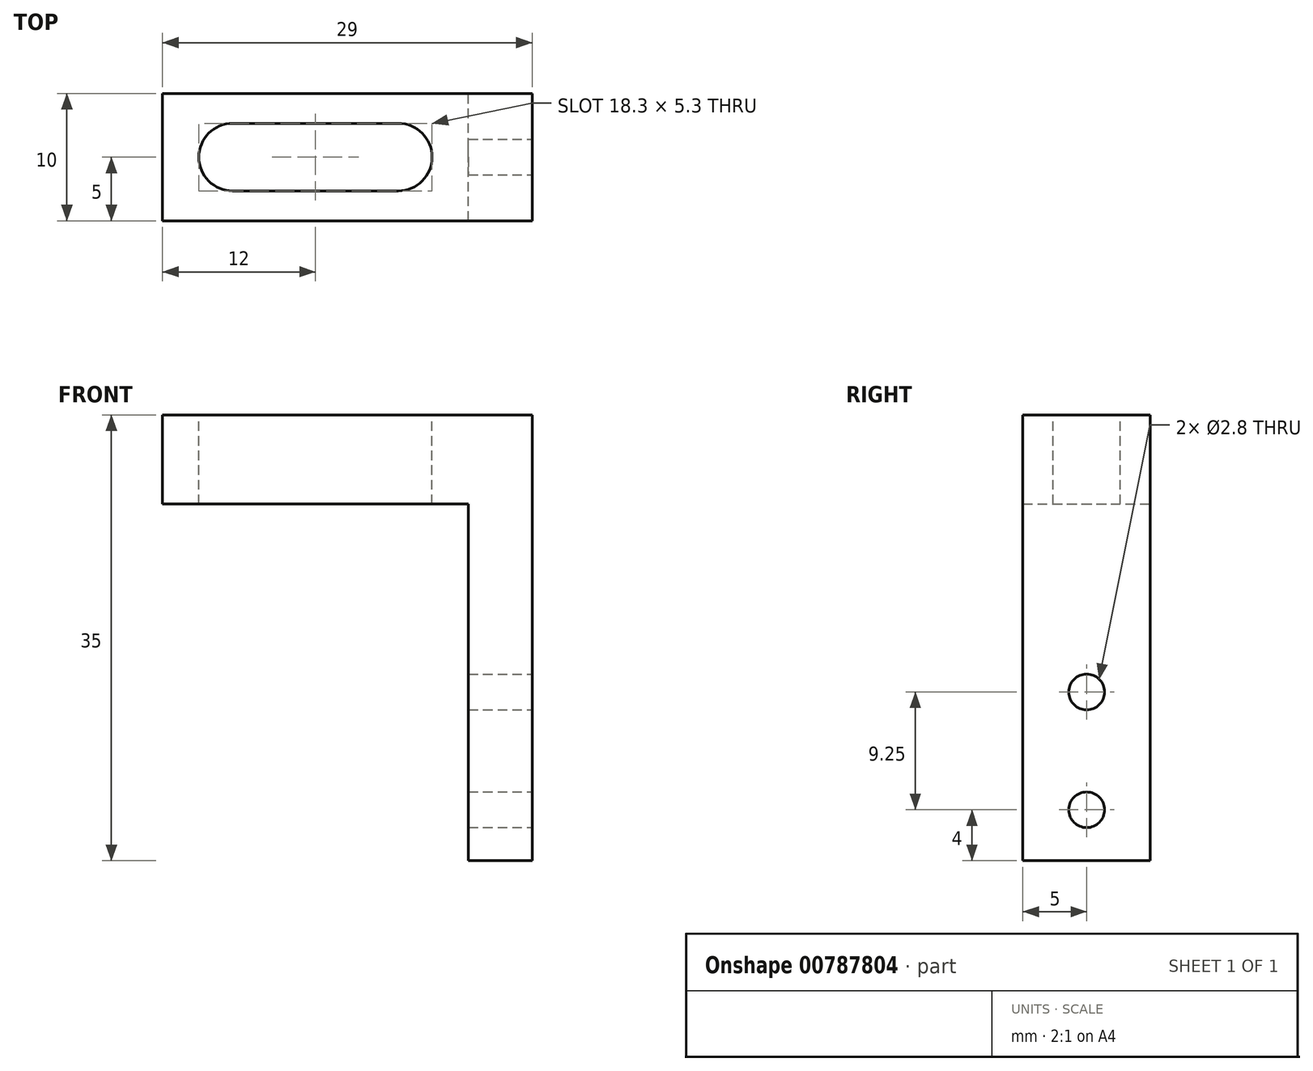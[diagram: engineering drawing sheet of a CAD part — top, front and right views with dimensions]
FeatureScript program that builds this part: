
annotation { "Feature Type Name" : "Feature", "Feature Type Description" : "" }
export const myFeature = defineFeature(function(context is Context, id is Id, definition is map)
    precondition{}
    {
        {
            var Q0;
            Q0=qCreatedBy(makeId("Front.planeOp"),FACE);
            var sketch = newSketch(context, id + "F0", { "sketchPlane" : qUnion([Q0])});
            skLineSegment(sketch, "E0", {"start": v(0, 0) * mm, "end": v(29, 0) * mm});
            skLineSegment(sketch, "E1", {"start": v(29, 0) * mm, "end": v(29, -35) * mm});
            skLineSegment(sketch, "E2", {"start": v(29, -35) * mm, "end": v(24, -35) * mm});
            skLineSegment(sketch, "E3", {"start": v(24, -35) * mm, "end": v(24, -7) * mm});
            skLineSegment(sketch, "E4", {"start": v(24, -7) * mm, "end": v(0, -7) * mm});
            skLineSegment(sketch, "E5", {"start": v(0, -7) * mm, "end": v(0, 0) * mm});
            skSolve(sketch);
        }
        {
            var Q0;
            Q0=makeQuery(id+"F0.imprint","IMPRINT",FACE,{"disambiguationData":[TD([[makeQuery(id+"F0.imprint","IMPRINT",EDGE,{"derivedFrom":sQuery(id+"F0.wireOp",EDGE,"E0")}),-1.0]])]});
            extrude(context, id + "F1", {"entities" : qUnion([Q0]), "depth" : 10 * mm, "offsetDistance" : 25 * mm});
        }
        {
            var Q0;
            Q0=makeQuery(id+"F1.opExtrude","SWEPT_FACE",FACE,{"disambiguationData":[OSD([sQuery(id+"F0.wireOp",EDGE,"E0")])]});
            var sketch = newSketch(context, id + "F2", { "sketchPlane" : qUnion([Q0])});
            skLineSegment(sketch, "E6.bottom", {"start": v(5.5, -7.65) * mm, "end": v(18.5, -7.65) * mm});
            skLineSegment(sketch, "E6.top", {"start": v(5.5, -2.35) * mm, "end": v(18.5, -2.35) * mm});
            skLineSegment(sketch, "E6.left", {"start": v(5.5, -7.65) * mm, "end": v(5.5, -2.35) * mm});
            skLineSegment(sketch, "E6.right", {"start": v(18.5, -7.65) * mm, "end": v(18.5, -2.35) * mm});
            skArc(sketch, "E7", {"start": v(5.5, -2.35) * mm, "mid": v(2.85, -5) * mm, "end": v(5.5, -7.65) * mm});
            skArc(sketch, "E8", {"start": v(18.5, -7.65) * mm, "mid": v(21.15, -5) * mm, "end": v(18.5, -2.35) * mm});
            skSolve(sketch);
        }
        {
            var Q0;
            Q0=makeQuery(id+"F2.imprint","IMPRINT",FACE,{"disambiguationData":[TD([[makeQuery(id+"F2.imprint","IMPRINT",EDGE,{"derivedFrom":sQuery(id+"F2.wireOp",EDGE,"E6.bottom")}),1.0]])]});
            var Q1;
            Q1=makeQuery(id+"F2.imprint","IMPRINT",FACE,{"disambiguationData":[TD([[makeQuery(id+"F2.imprint","IMPRINT",EDGE,{"derivedFrom":sQuery(id+"F2.wireOp",EDGE,"E6.left")}),1.0]])]});
            var Q2;
            Q2=makeQuery(id+"F2.imprint","IMPRINT",FACE,{"disambiguationData":[TD([[makeQuery(id+"F2.imprint","IMPRINT",EDGE,{"derivedFrom":sQuery(id+"F2.wireOp",EDGE,"E6.right")}),-1.0]])]});
            extrude(context, id + "F3", {"entities" : qUnion([Q0, Q1, Q2]), "operationType" : NewBodyOperationType.REMOVE, "endBound" : BoundingType.UP_TO_NEXT, "oppositeDirection" : true, "depth" : 25 * mm, "offsetDistance" : 25 * mm});
        }
        {
            var Q0;
            Q0=makeQuery(id+"F1.opExtrude","SWEPT_FACE",FACE,{"disambiguationData":[OSD([sQuery(id+"F0.wireOp",EDGE,"E1")])]});
            var sketch = newSketch(context, id + "F4", { "sketchPlane" : qUnion([Q0])});
            skCircle(sketch, "E9", {"center": v(-5, -31) * mm, "radius": 1.4 * mm});
            skPoint(sketch, "E9.centerSnap0", {"position": v(-5, -35) * mm});
            skCircle(sketch, "E10", {"center": v(-5, -21.75) * mm, "radius": 1.4 * mm});
            skSolve(sketch);
        }
        {
            var Q0;
            Q0=makeQuery(id+"F4.imprint","IMPRINT",FACE,{"disambiguationData":[TD([[makeQuery(id+"F4.imprint","IMPRINT",EDGE,{"derivedFrom":sQuery(id+"F4.wireOp",EDGE,"E10")}),1.0]])]});
            var Q1;
            Q1=makeQuery(id+"F4.imprint","IMPRINT",FACE,{"disambiguationData":[TD([[makeQuery(id+"F4.imprint","IMPRINT",EDGE,{"derivedFrom":sQuery(id+"F4.wireOp",EDGE,"E9")}),1.0]])]});
            extrude(context, id + "F5", {"entities" : qUnion([Q0, Q1]), "operationType" : NewBodyOperationType.REMOVE, "endBound" : BoundingType.UP_TO_NEXT, "oppositeDirection" : true, "depth" : 25 * mm, "offsetDistance" : 25 * mm});
        }
    });
